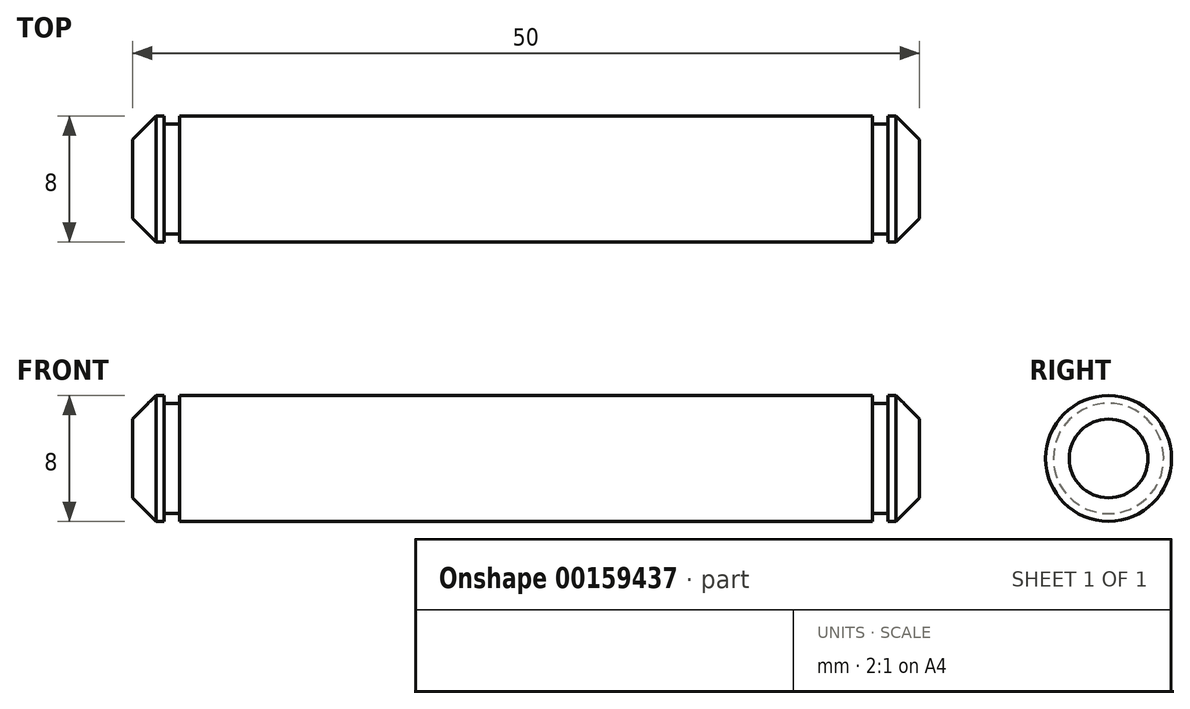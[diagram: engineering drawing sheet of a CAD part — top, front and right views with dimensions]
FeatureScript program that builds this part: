
annotation { "Feature Type Name" : "Feature", "Feature Type Description" : "" }
export const myFeature = defineFeature(function(context is Context, id is Id, definition is map)
    precondition{}
    {
        {
            var Q0;
            Q0=qCreatedBy(makeId("Front.planeOp"),FACE);
            var sketch = newSketch(context, id + "F0", { "sketchPlane" : qUnion([Q0])});
            skLineSegment(sketch, "E0", {"start": v(0, 0) * mm, "end": v(50, 0) * mm, "construction": true});
            skLineSegment(sketch, "E1", {"start": v(25, -4) * mm, "end": v(25, 4) * mm, "construction": true});
            skPoint(sketch, "E1.startSnap0", {"position": v(25, 0) * mm});
            skLineSegment(sketch, "E2.bottom", {"start": v(0, 0) * mm, "end": v(25, 0) * mm});
            skLineSegment(sketch, "E2.top", {"start": v(0, 4) * mm, "end": v(2, 4) * mm});
            skLineSegment(sketch, "E2.left", {"start": v(0, 0) * mm, "end": v(0, 4) * mm});
            skLineSegment(sketch, "E2.right", {"start": v(25, 0) * mm, "end": v(25, 4) * mm});
            skLineSegment(sketch, "E3.top", {"start": v(2, 3.5) * mm, "end": v(3, 3.5) * mm});
            skLineSegment(sketch, "E3.left", {"start": v(2, 4) * mm, "end": v(2, 3.5) * mm});
            skLineSegment(sketch, "E3.right", {"start": v(3, 4) * mm, "end": v(3, 3.5) * mm});
            skLineSegment(sketch, "E4.trimOffspring", {"start": v(3, 4) * mm, "end": v(25, 4) * mm});
            skLineSegment(sketch, "E5.MirrorCS", {"start": v(47, 4) * mm, "end": v(25, 4) * mm});
            skLineSegment(sketch, "E6.MirrorCS", {"start": v(47, 4) * mm, "end": v(47, 3.5) * mm});
            skLineSegment(sketch, "E7.MirrorCS", {"start": v(48, 3.5) * mm, "end": v(47, 3.5) * mm});
            skLineSegment(sketch, "E8.MirrorCS", {"start": v(48, 4) * mm, "end": v(48, 3.5) * mm});
            skLineSegment(sketch, "E9.MirrorCS", {"start": v(50, 4) * mm, "end": v(48, 4) * mm});
            skLineSegment(sketch, "E10.MirrorCS", {"start": v(50, 0) * mm, "end": v(50, 4) * mm});
            skLineSegment(sketch, "E11.MirrorCS", {"start": v(50, 0) * mm, "end": v(25, 0) * mm});
            skSolve(sketch);
        }
        {
            var Q0;
            Q0 = qSketchRegion(id + "F0", true);
            var Q1;
            Q1=sQuery(id+"F0.wireOp",EDGE,"E2.bottom");
            revolve(context, id + "F1", {"entities" : qUnion([Q0]), "axis" : qUnion([Q1]), "revolveType" : RevolveType.FULL});
        }
        {
            var Q0;
            Q0=makeQuery(id+"F1.opRevolve","SWEPT_FACE",FACE,{"disambiguationData":[OSD([sQuery(id+"F0.wireOp",EDGE,"E10.MirrorCS")])]});
            var Q1;
            Q1=makeQuery(id+"F1.opRevolve","SWEPT_EDGE",EDGE,{"disambiguationData":[OSD([sQuery(id+"F0.wireOp",EDGE,"E2.top"),sQuery(id+"F0.wireOp",EDGE,"E2.left")])]});
            chamfer(context, id + "F2", {"entities" : qUnion([Q0, Q1]), "width" : 1.5 * mm, "tangentPropagation" : true});
        }
    });
